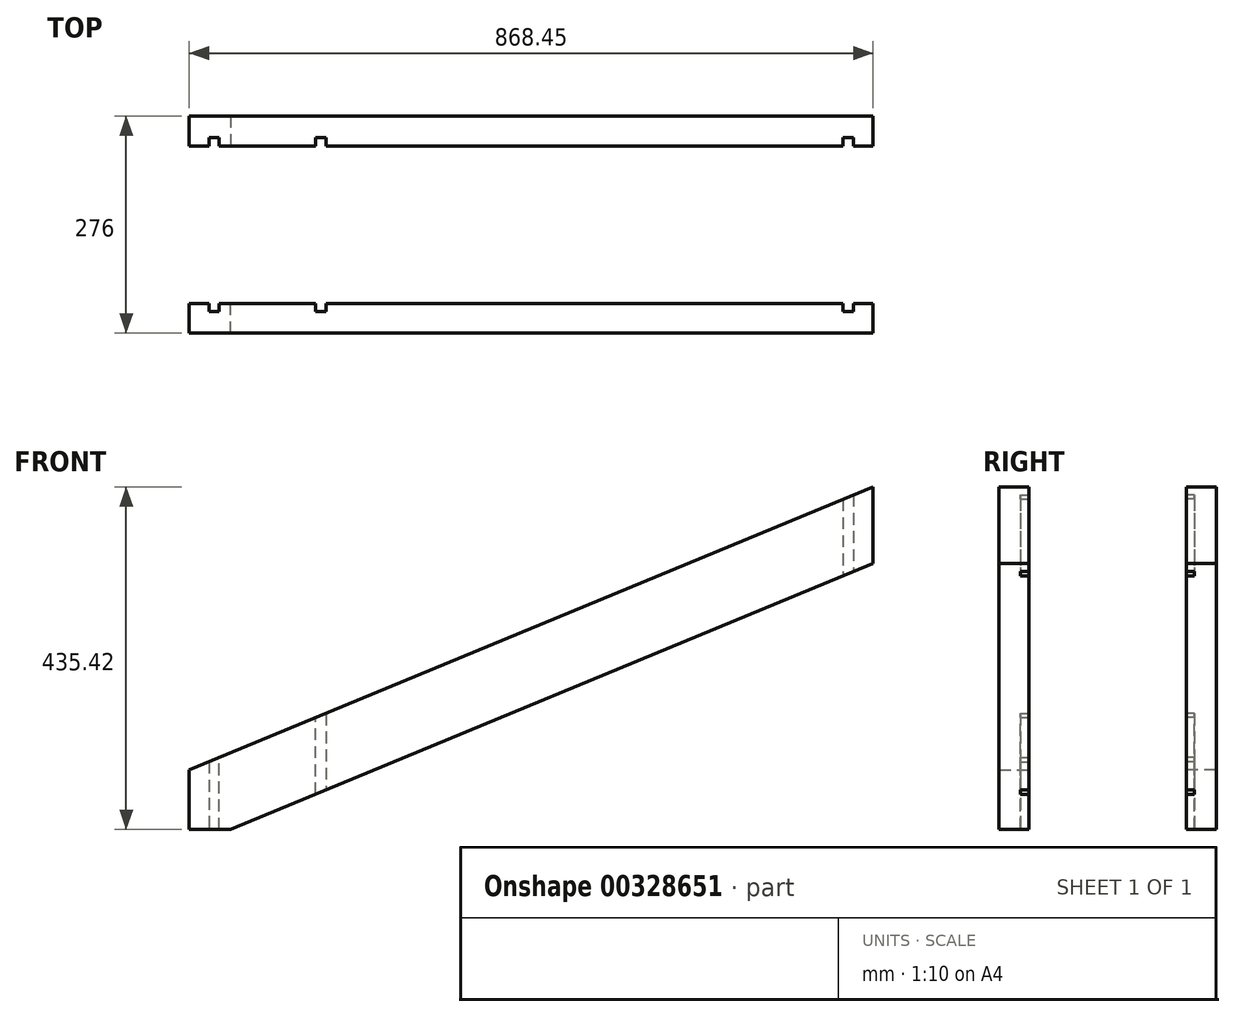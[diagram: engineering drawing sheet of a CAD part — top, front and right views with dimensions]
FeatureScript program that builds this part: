
annotation { "Feature Type Name" : "Feature", "Feature Type Description" : "" }
export const myFeature = defineFeature(function(context is Context, id is Id, definition is map)
    precondition{}
    {
        {
            var Q0;
            Q0=qCreatedBy(makeId("Front.planeOp"),FACE);
            var sketch = newSketch(context, id + "F0", { "sketchPlane" : qUnion([Q0])});
            skLineSegment(sketch, "E0", {"start": v(0, 0) * mm, "end": v(0, 75.7) * mm});
            skLineSegment(sketch, "E1", {"start": v(0, 0) * mm, "end": v(52.43, 0) * mm});
            skLineSegment(sketch, "E2", {"start": v(52.43, 0) * mm, "end": v(868.45, 338) * mm});
            skLineSegment(sketch, "E3", {"start": v(868.45, 338) * mm, "end": v(868.45, 435.42) * mm});
            skLineSegment(sketch, "E4", {"start": v(0, 75.7) * mm, "end": v(868.45, 435.42) * mm});
            skSolve(sketch);
        }
        {
            var Q0;
            Q0=qSketchRegion(id+"F0",true);
            extrude(context, id + "F1", {"entities" : qUnion([Q0]), "oppositeDirection" : true, "depth" : 38 * mm});
        }
        {
            var Q0;
            Q0=makeQuery(id+"F1.opExtrude","CAP_FACE",FACE,{"disambiguationData":[OSD([sQuery(id+"F0.wireOp",EDGE,"E0"),sQuery(id+"F0.wireOp",EDGE,"E1"),sQuery(id+"F0.wireOp",EDGE,"E2"),sQuery(id+"F0.wireOp",EDGE,"E3"),sQuery(id+"F0.wireOp",EDGE,"E4")])],"isStart":true});
            var sketch = newSketch(context, id + "F2", { "sketchPlane" : qUnion([Q0])});
            skLineSegment(sketch, "E5", {"start": v(830.45, 419.68) * mm, "end": v(830.45, 322.27) * mm});
            skLineSegment(sketch, "E6", {"start": v(843.45, 425.07) * mm, "end": v(843.45, 327.65) * mm});
            skLineSegment(sketch, "E7", {"start": v(843.45, 327.65) * mm, "end": v(830.45, 322.27) * mm});
            skLineSegment(sketch, "E8", {"start": v(173.45, 147.54) * mm, "end": v(173.45, 50.13) * mm});
            skLineSegment(sketch, "E9", {"start": v(173.45, 50.13) * mm, "end": v(160.45, 44.74) * mm});
            skLineSegment(sketch, "E10", {"start": v(160.45, 44.74) * mm, "end": v(160.45, 142.16) * mm});
            skLineSegment(sketch, "E11", {"start": v(160.45, 142.16) * mm, "end": v(173.45, 147.54) * mm});
            skLineSegment(sketch, "E12", {"start": v(38, 0) * mm, "end": v(38, 91.44) * mm});
            skLineSegment(sketch, "E13", {"start": v(38, 91.44) * mm, "end": v(25, 86.06) * mm});
            skLineSegment(sketch, "E14", {"start": v(25, 86.06) * mm, "end": v(25, 0) * mm});
            skLineSegment(sketch, "E15", {"start": v(25, 0) * mm, "end": v(38, 0) * mm});
            skLineSegment(sketch, "E16", {"start": v(830.45, 419.68) * mm, "end": v(843.45, 425.07) * mm});
            skSolve(sketch);
        }
        {
            var Q0;
            Q0=qSketchRegion(id+"F2",true);
            extrude(context, id + "F3", {"entities" : qUnion([Q0]), "operationType" : NewBodyOperationType.REMOVE, "oppositeDirection" : true, "depth" : 10.5 * mm});
        }
        {
            var Q0;
            {var subQ0=sQuery(id+"F0.wireOp",EDGE,"E2");var subQ1=sQuery(id+"F0.wireOp",EDGE,"E4");Q0=makeQuery(id+"F3.boolean.opBoolean","SPLIT",FACE,{"disambiguationData":[TD([makeQuery(id+"F3.opExtrude","SWEPT_FACE",FACE,{"disambiguationData":[OSD([sQuery(id+"F2.wireOp",EDGE,"E5")])]})])],"derivedFrom":makeQuery(id+"F1.opExtrude","CAP_FACE",FACE,{"disambiguationData":[OSD([sQuery(id+"F0.wireOp",EDGE,"E0"),sQuery(id+"F0.wireOp",EDGE,"E1"),subQ0,sQuery(id+"F0.wireOp",EDGE,"E3"),subQ1])],"isStart":true})});}
            cPlane(context, id + "F4", {"entities" : qUnion([Q0]), "cplaneType" : CPlaneType.OFFSET, "offset" : 100 * mm, "width" : 150 * mm, "height" : 150 * mm});
        }
        {
            var Q0;
            Q0=makeQuery(id+"F1.opExtrude","SWEPT_BODY",BODY,{"disambiguationData":[OSD([sQuery(id+"F0.wireOp",EDGE,"E0"),sQuery(id+"F0.wireOp",EDGE,"E1"),sQuery(id+"F0.wireOp",EDGE,"E2"),sQuery(id+"F0.wireOp",EDGE,"E3"),sQuery(id+"F0.wireOp",EDGE,"E4")])]});
            var Q1;
            Q1=qCreatedBy(id+"F4.planeOp",FACE);
            mirror(context, id + "F5", {"entities" : qUnion([Q0]), "mirrorPlane" : qUnion([Q1])});
        }
    });
